# Revit family: oventrop_cocon-qfc_1146149-56rfa
name_source: partatom
category: Арматура трубопроводов
revit_build: Autodesk Revit 2017 (Build: 20160225_1515(x64)
units: mm (PartAtom-declared; Revit-internal decimal feet)

## family parameters
Всегда вертикально = Да
Заголовок OmniClass = Adjusting/Controlling Valves for Liquid Services
На основе рабочей плоскости = Нет
Номер OmniClass = 23.65.55.14.17
Общий = Нет
При загрузке вырезать с полостями = Нет
Размер круглого соединителя = Использовать радиус
Тип детали = Клапан - Вставляется

## types (8) — shared parameters
Aluminium = Color RGB 140-140-140
Angle = 60.00°
Article Description = Flow Control valve
Article Type = Cocon QFC 11461
Bonnet = Color RGB 35-35-35
Bronze = Color RGB 156-122-90
Custom = Нет
EMCS Version = 2.0
ETIM Article Class = EC011435
Family Version = 10.14
IFCExportAs = IfcValveType
IFCExportType = REGULATING
L2 = 38 мм
Lgt1 = 3 мм
MEPcontent Class = VALVE_CONTROL
Manufacturer URL = http://www.oventrop.de
Product Line = Oventrop
Ra1 = 8 мм
Ra2 = 6 мм
Ra3 = 5 мм
Ra4 = 15 мм
Revit Version = 2015
r1 = 2 мм
r2 = 3 мм
Группа модели = Cocon QFC 11461
Изготовитель = Oventrop
Описание = Flow Control valve

## per-type parameters (varying)
- DN 40: Arrow1=4 мм; FlangeDiameter=150 мм; GTIN=4026755372465; Hb1=285 мм; Hb3=11 мм; Hb4=5 мм; Hb5=4 мм; Hb6=10 мм; Height=250 мм; L1=200 мм; Length=200 мм; Length_B=11 мм; Length_C=19 мм; Length_D=14 мм; Lgt2=12 мм; Lgt3=25 мм; Manufacturer Art. No.=1146149; Nominal Diameter=40 мм; OuterDiameter=48 мм; Rad1=50 мм; Rad2=75 мм; Rad3=38 мм; Rad4=32 мм; RadiusPressure=22 мм; Rb1=32 мм; Safe_Length=32 мм; URL=www.stabiplan.com
- DN 50: Arrow1=5 мм; FlangeDiameter=165 мм; GTIN=4026755355246; Hb1=308 мм; Hb3=15 мм; Hb4=7 мм; Hb5=5 мм; Hb6=14 мм; Height=270 мм; L1=230 мм; Length=230 мм; Length_B=12 мм; Length_C=21 мм; Length_D=15 мм; Lgt2=14 мм; Lgt3=29 мм; Manufacturer Art. No.=1146150; Nominal Diameter=50 мм; OuterDiameter=60 мм; Rad1=55 мм; Rad2=83 мм; Rad3=42 мм; Rad4=36 мм; RadiusPressure=26 мм; Rb1=36 мм; Safe_Length=36 мм; URL=www.stabiplan.com
- DN 65: Arrow1=6 мм; FlangeDiameter=185 мм; GTIN=4026755355253; Hb1=423 мм; Hb3=35 мм; Hb4=16 мм; Hb5=12 мм; Hb6=32 мм; Height=370 мм; L1=290 мм; Length=290 мм; Length_B=17 мм; Length_C=28 мм; Length_D=21 мм; Lgt2=17 мм; Lgt3=36 мм; Manufacturer Art. No.=1146151; Nominal Diameter=65 мм; OuterDiameter=76 мм; Rad1=61 мм; Rad2=93 мм; Rad3=47 мм; Rad4=40 мм; RadiusPressure=30 мм; Rb1=40 мм; Safe_Length=40 мм; URL=www.stabiplan.com
- DN 80: Arrow1=6 мм; FlangeDiameter=200 мм; GTIN=4026755355260; Hb1=441 мм; Hb3=38 мм; Hb4=17 мм; Hb5=13 мм; Hb6=35 мм; Height=385 мм; L1=310 мм; Length=310 мм; Length_B=18 мм; Length_C=29 мм; Length_D=22 мм; Lgt2=19 мм; Lgt3=39 мм; Manufacturer Art. No.=1146152; Nominal Diameter=80 мм; OuterDiameter=89 мм; Rad1=66 мм; Rad2=100 мм; Rad3=51 мм; Rad4=43 мм; RadiusPressure=33 мм; Rb1=43 мм; Safe_Length=43 мм; URL=www.stabiplan.com
- DN 100: Arrow1=7 мм; FlangeDiameter=220 мм; GTIN=4026755355277; Hb1=464 мм; Hb3=42 мм; Hb4=19 мм; Hb5=14 мм; Hb6=38 мм; Height=405 мм; L1=350 мм; Length=350 мм; Length_B=19 мм; Length_C=31 мм; Length_D=23 мм; Lgt2=21 мм; Lgt3=44 мм; Manufacturer Art. No.=1146153; Nominal Diameter=100 мм; OuterDiameter=114 мм; Rad1=73 мм; Rad2=110 мм; Rad3=56 мм; Rad4=47 мм; RadiusPressure=37 мм; Rb1=47 мм; Safe_Length=47 мм; URL=www.stabiplan.com
- DN 125: Arrow1=8 мм; FlangeDiameter=250 мм; GTIN=4026755355284; Hb1=596 мм; Hb3=65 мм; Hb4=30 мм; Hb5=22 мм; Hb6=59 мм; Height=520 мм; L1=400 мм; Length=400 мм; Length_B=24 мм; Length_C=40 мм; Length_D=30 мм; Lgt2=24 мм; Lgt3=50 мм; Manufacturer Art. No.=1146154; Nominal Diameter=125 мм; OuterDiameter=140 мм; Rad1=83 мм; Rad2=125 мм; Rad3=63 мм; Rad4=54 мм; RadiusPressure=34 мм; Rb1=54 мм; Safe_Length=54 мм; URL=www.stabiplan.com
- DN 150: Arrow1=10 мм; FlangeDiameter=285 мм; GTIN=4026755355291; Hb1=596 мм; Hb3=65 мм; Hb4=30 мм; Hb5=22 мм; Hb6=59 мм; Height=520 мм; L1=480 мм; Length=480 мм; Length_B=24 мм; Length_C=40 мм; Length_D=30 мм; Lgt2=29 мм; Lgt3=60 мм; Manufacturer Art. No.=1146155; Nominal Diameter=150 мм; OuterDiameter=168 мм; Rad1=94 мм; Rad2=143 мм; Rad3=72 мм; Rad4=61 мм; RadiusPressure=41 мм; Rb1=61 мм; Safe_Length=61 мм; URL=http://file-system.ru
- DN 200: Arrow1=12 мм; FlangeDiameter=340 мм; GTIN=4026755391176; Hb1=648 мм; Hb3=74 мм; Hb4=34 мм; Hb5=25 мм; Hb6=67 мм; Height=565 мм; L1=600 мм; Length=600 мм; Length_B=26 мм; Length_C=43 мм; Length_D=32 мм; Lgt2=36 мм; Lgt3=75 мм; Manufacturer Art. No.=1146156; Nominal Diameter=200 мм; OuterDiameter=219 мм; Rad1=112 мм; Rad2=170 мм; Rad3=86 мм; Rad4=73 мм; RadiusPressure=53 мм; Rb1=73 мм; Safe_Length=73 мм; URL=www.stabiplan.com

## geometry (parser evidence)
native form markers: Sweep x3
no freeform markers — native parametric forms only
